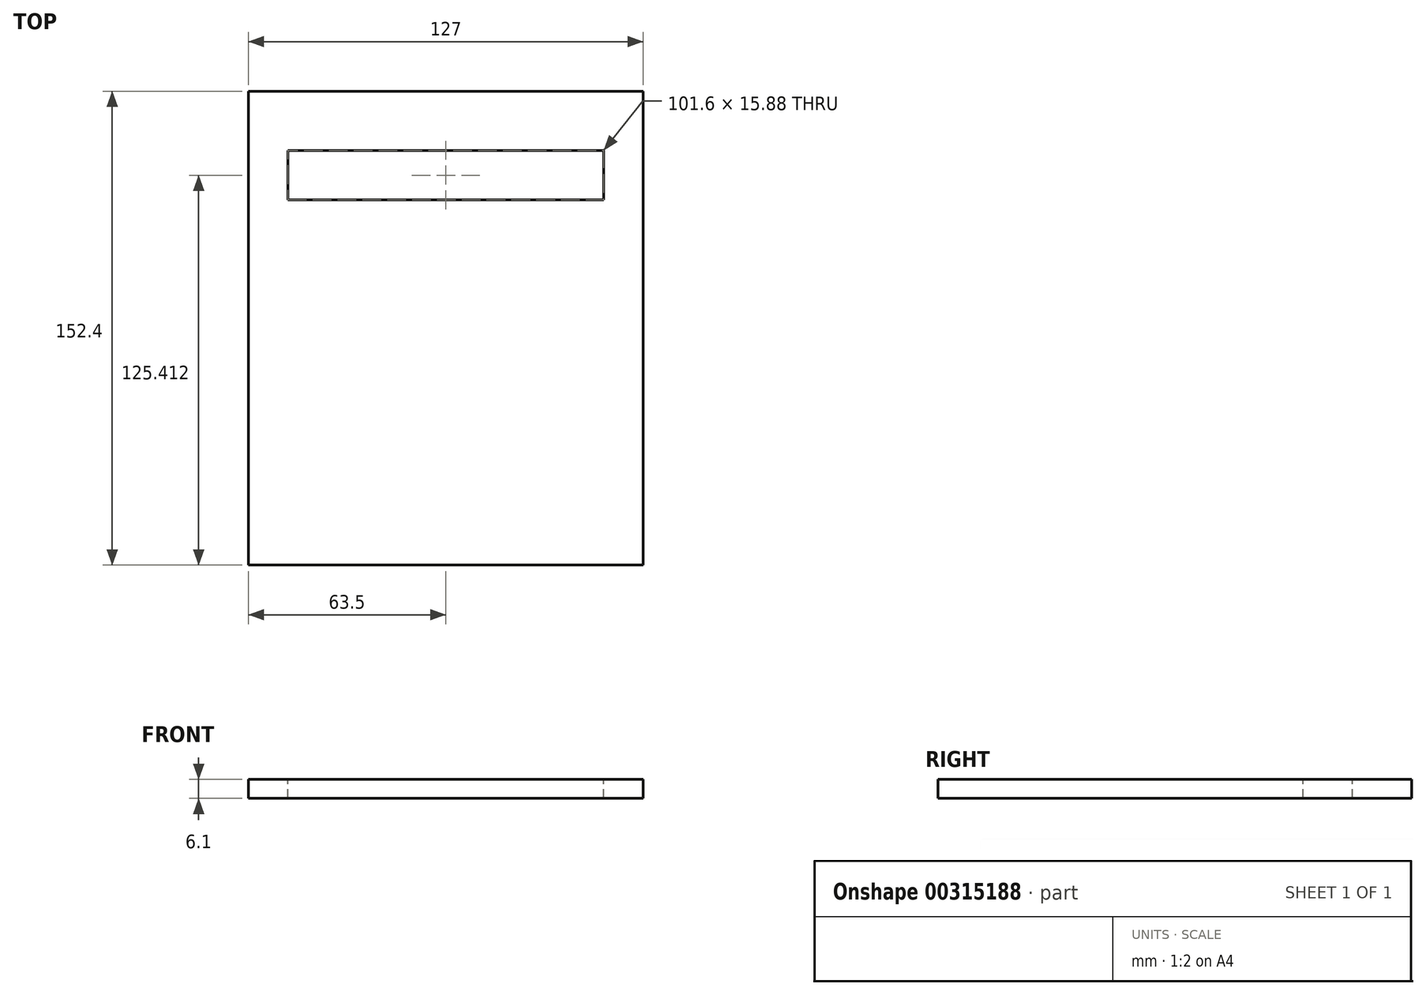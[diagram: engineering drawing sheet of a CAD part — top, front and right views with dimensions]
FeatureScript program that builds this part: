
annotation { "Feature Type Name" : "Feature", "Feature Type Description" : "" }
export const myFeature = defineFeature(function(context is Context, id is Id, definition is map)
    precondition{}
    {
        {
            var Q0;
            Q0=qCreatedBy(makeId("Top.planeOp"),FACE);
            var sketch = newSketch(context, id + "F0", { "sketchPlane" : qUnion([Q0])});
            skLineSegment(sketch, "E0", {"start": v(0, 76.2) * mm, "end": v(-63.5, 76.2) * mm});
            skLineSegment(sketch, "E1", {"start": v(-63.5, 76.2) * mm, "end": v(-63.5, -76.2) * mm});
            skLineSegment(sketch, "E2", {"start": v(-63.5, -76.2) * mm, "end": v(0, -76.2) * mm});
            skLineSegment(sketch, "E3", {"start": v(0, 76.2) * mm, "end": v(0, -76.2) * mm, "construction": true});
            skLineSegment(sketch, "E4.MirrorCS", {"start": v(0, 76.2) * mm, "end": v(63.5, 76.2) * mm});
            skLineSegment(sketch, "E5.MirrorCS", {"start": v(63.5, 76.2) * mm, "end": v(63.5, -76.2) * mm});
            skLineSegment(sketch, "E6.MirrorCS", {"start": v(63.5, -76.2) * mm, "end": v(0, -76.2) * mm});
            skLineSegment(sketch, "E7.bottom", {"start": v(-50.8, 41.27) * mm, "end": v(50.8, 41.27) * mm});
            skLineSegment(sketch, "E7.top", {"start": v(-50.8, 57.15) * mm, "end": v(50.8, 57.15) * mm});
            skLineSegment(sketch, "E7.left", {"start": v(-50.8, 41.27) * mm, "end": v(-50.8, 57.15) * mm});
            skLineSegment(sketch, "E7.right", {"start": v(50.8, 41.27) * mm, "end": v(50.8, 57.15) * mm});
            skPoint(sketch, "E7.middle", {"position": v(0, 49.21) * mm});
            skLineSegment(sketch, "E8.0", {"start": v(-57.4, 76.2) * mm, "end": v(-57.4, -76.2) * mm});
            skSolve(sketch);
        }
        {
            var Q0;
            Q0 = qSketchRegion(id + "F0", true);
            extrude(context, id + "F1", {"entities" : qUnion([Q0]), "oppositeDirection" : true, "depth" : 6.1 * mm});
        }
    });
